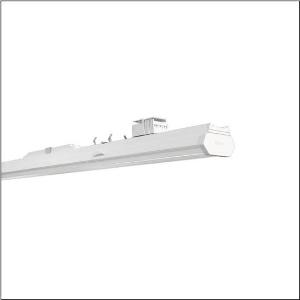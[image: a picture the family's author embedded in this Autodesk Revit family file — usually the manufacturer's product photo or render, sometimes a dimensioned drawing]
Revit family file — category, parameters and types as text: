
# Revit family: licross_11_protected_ho_51td1bdn4e5m
name_source: partatom
category: Lighting Fixtures
units: mm (PartAtom-declared; Revit-internal decimal feet)

## family parameters
Cut with Voids When Loaded = No
Host = Face
Light Source = No
Part Type = Normal
Room Calculation Point = No
Round Connector Dimension = Use Diameter
Shared = No

## types (1)
- --- (1 x LED, 14500 lm, 87.3 W, 4000K)
    Apparent Load = 87 VA
    CIE Flux Codes = 54 82 95 97 100
    Color Rendering = 80
    Color Temperature = 4000K
    Default Elevation = 1800 mm
    Description = Licross 11 Protected HO, luminaire insert, of sheet steel, galvanised, coil coated, white, length: 1.500mm, width: 90mm, height: 101mm, LED rated luminous flux: 14.500lm, light colour: 840, SDCM (Standard Deviation of Colour Matching)MacAdam ≤ 2 SDCM (initial), control gear: DALI 2, with plug, 5-pole, with phase selection, mains connection: 220..240V, AC, 50/60Hz, rated input power: 87W, internal wiring halogen-free, primary optical cover: cover, of PMMA, light emission: direct distribution, primary light characteristic: symmetric, protection rating (complete): IP54, insulation class (complete): insulation class I (protective earthing), certification: CE, ENEC, VDE, UKCA, protection symbol: D if used in an environment with non-conductive dust loads with corresponding accessories, impact resistance: IK06, permissible ambient temperature for indoor applications: -25..+30°C, corresponds to IFS (International Featured Standards) requirements for safety and quality in the food industry, reducing of maximum allowable ambient temperature of 5°C with ceiling mounting, LABS conformity tested according to VDMA 24364:2018-05, The light source and the operating device comply with the requirements of the Ecodesign Regulation (EU) 2019/2020 and are replaceable in accordance with this regulation, packaging unit: 1 piece
    Height = 92 mm
    Lamp = 1 x LED
    Lamp Light Flux = 14500 lm
    Lamp Power = 87.3 W
    Lamp count = 1
    Length = 1500 mm
    Luminous efficacy = 166 lm/W
    Manufacturer = Siteco
    ModVariant = No
    Model = 51TD1BDN4E5M
    Mounting Place = Ceiling
    Mounting Type = Pendant
    Number of Poles = 1
    OnlyDefault = Yes
    Power Factor = 1
    Product Name = Licross 11 Protected HO
    Product group = luminaire insert | ceiling pendant
    ProductGroupID = 901
    Protection Class = Protection class I
    Protection Degree = IP 54
    RLX_Detail_Level = 1
    RLX_Emergency_Light_Flux = 0 lm
    RLX_Emergency_Type = 0
    RLX_Emergency_Type_DB = No
    RlxData = <blob elided: 24625 chars, md5=54bef6b9>
    Socket = socket
    Standby Power = 0 W
    System Light Flux = 14500 lm
    System Power = 87 W
    Type Comments = factory setting: luminous flux: 100 % | dim-lin: 254 | 589 mA
    Type Image = l_1256145.jpg
    URL = http://relux.com
    VarID = @adj_031979
    Voltage = 0 V
    Weight = 0.00 kg
    Width = 88 mm

## geometry (parser evidence)
native form markers: Blend x4, Sweep x10
no freeform markers — native parametric forms only
